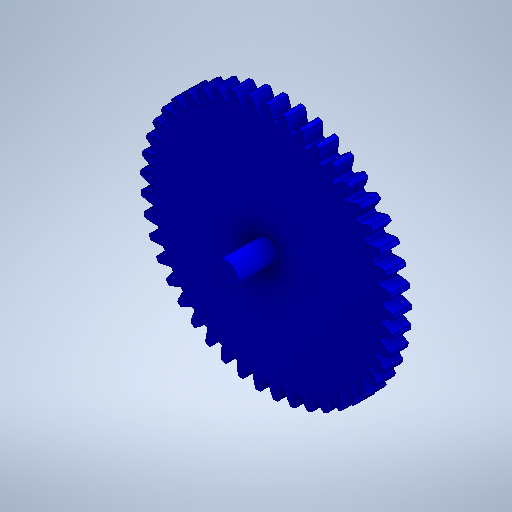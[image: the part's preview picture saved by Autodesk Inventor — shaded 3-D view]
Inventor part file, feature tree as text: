
AUTODESK INVENTOR PART (.ipt)
format: ipt  version: 2025.2 (Build 292293000, 293)  size: 481,280 bytes
history: native  units: mm (DEFAULTED — no unit token found)
features: plane x3, other x3, extrude x2, sketch x2
ambient origin geometry x8: Origin, YZ Plane, XZ Plane, XY Plane, X Axis, Y Axis, Z Axis, Center Point
bodies: Solid1 (feature_tree)
feature tree (10):
  extrude  "Extrusion1"  Depth=7.0mm TaperAngle=0.0deg
  plane  "Work Plane2"
  plane  "Work Plane8"
  plane  "Work Plane9"
  other  "Spur Gear"
  extrude  "Extrusion2"  Depth=10.0mm TaperAngle=0.0deg
  sketch  "Sketch1"  dims[d0=94.0mm d1=7.0mm d2=0.0mm]
  other  "Srf1"
  sketch  "Sketch3"  dims[d3=90.0mm d4=10.0mm d5=0.0mm d16=60.0mm d17=0.0mm d34=0.698132mm d39=0.0mm d41=0.0mm d43=60.0mm d46=60.0mm d47=0.0mm d48=0.0mm d49=8.0mm d50=15.0mm d51=0.0mm d52=0.5mm d53=0.872665mm d54=0.5mm d55=0.872665mm]
  other  "Pitch Diameter"
